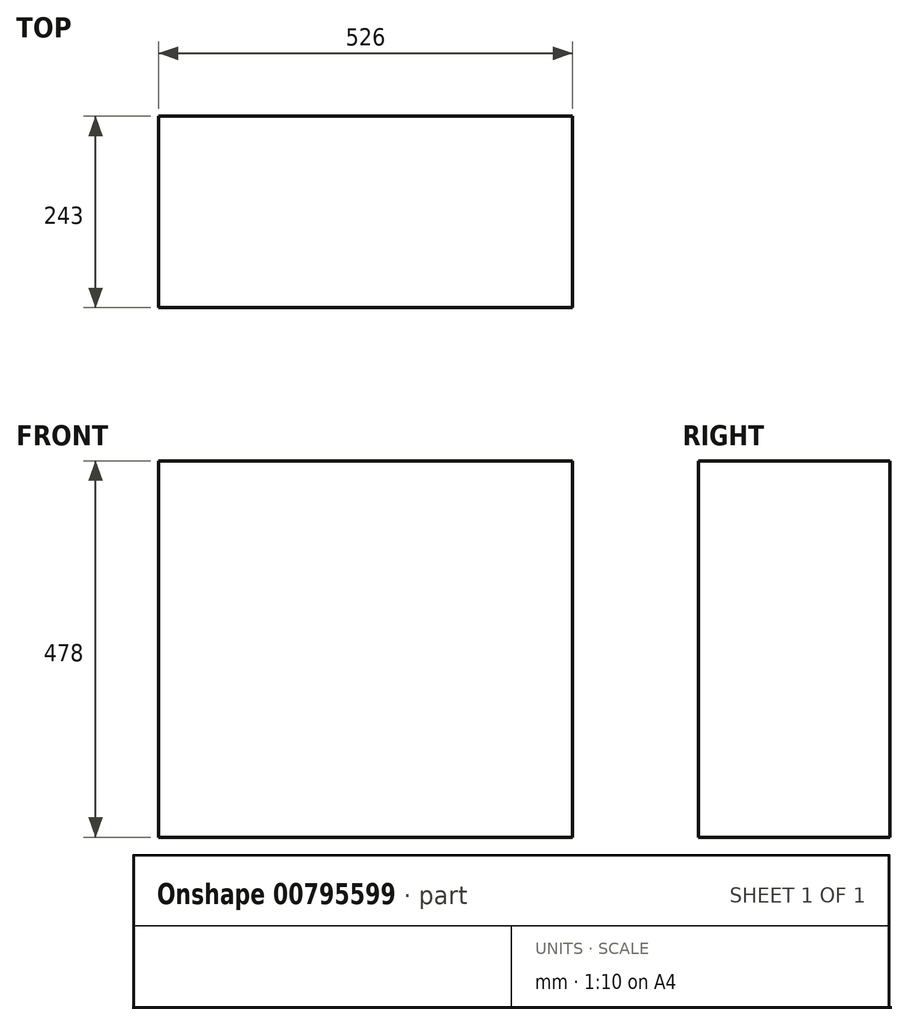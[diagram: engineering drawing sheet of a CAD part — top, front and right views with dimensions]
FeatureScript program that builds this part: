
annotation { "Feature Type Name" : "Feature", "Feature Type Description" : "" }
export const myFeature = defineFeature(function(context is Context, id is Id, definition is map)
    precondition{}
    {
        {
            var Q0;
            Q0=qCreatedBy(makeId("Top.planeOp"),FACE);
            var sketch = newSketch(context, id + "F0", { "sketchPlane" : qUnion([Q0])});
            skLineSegment(sketch, "E0.bottom", {"start": v(-263, 121.5) * mm, "end": v(263, 121.5) * mm});
            skLineSegment(sketch, "E0.top", {"start": v(-263, -121.5) * mm, "end": v(263, -121.5) * mm});
            skLineSegment(sketch, "E0.left", {"start": v(-263, 121.5) * mm, "end": v(-263, -121.5) * mm});
            skLineSegment(sketch, "E0.right", {"start": v(263, 121.5) * mm, "end": v(263, -121.5) * mm});
            skPoint(sketch, "E0.middle", {"position": v(0, 0) * mm});
            skSolve(sketch);
        }
        {
            var Q0;
            Q0=makeQuery(id+"F0.imprint","IMPRINT",FACE,{"disambiguationData":[TD([[makeQuery(id+"F0.imprint","IMPRINT",EDGE,{"derivedFrom":sQuery(id+"F0.wireOp",EDGE,"E0.bottom")}),-1.0]])]});
            extrude(context, id + "F1", {"entities" : qUnion([Q0]), "depth" : 478 * mm, "offsetDistance" : 25 * mm});
        }
    });
